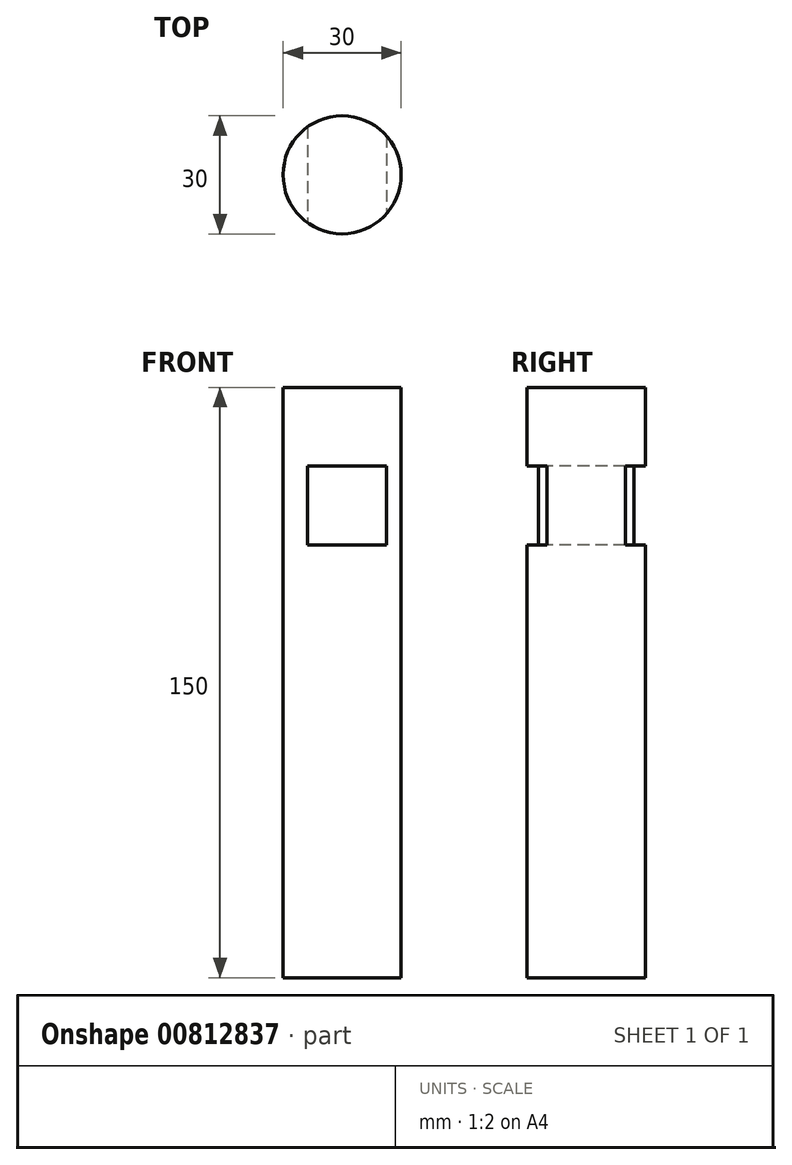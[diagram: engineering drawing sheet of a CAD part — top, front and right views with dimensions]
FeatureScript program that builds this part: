
annotation { "Feature Type Name" : "Feature", "Feature Type Description" : "" }
export const myFeature = defineFeature(function(context is Context, id is Id, definition is map)
    precondition{}
    {
        {
            var Q0;
            Q0=qCreatedBy(makeId("Top.planeOp"),FACE);
            var sketch = newSketch(context, id + "F0", { "sketchPlane" : qUnion([Q0])});
            skCircle(sketch, "E0", {"center": v(0, 0) * mm, "radius": 15 * mm});
            skSolve(sketch);
        }
        {
            var Q0;
            Q0=makeQuery(id+"F0.imprint","IMPRINT",FACE,{"disambiguationData":[TD([[makeQuery(id+"F0.imprint","IMPRINT",EDGE,{"derivedFrom":sQuery(id+"F0.wireOp",EDGE,"E0")}),1.0]])]});
            extrude(context, id + "F1", {"entities" : qUnion([Q0]), "depth" : 150 * mm, "offsetDistance" : 25 * mm});
        }
        {
            var Q0;
            Q0=qCreatedBy(makeId("Front.planeOp"),FACE);
            var sketch = newSketch(context, id + "F2", { "sketchPlane" : qUnion([Q0])});
            skLineSegment(sketch, "E1.bottom", {"start": v(-8.79, 130) * mm, "end": v(11.21, 130) * mm});
            skLineSegment(sketch, "E1.top", {"start": v(-8.79, 110) * mm, "end": v(11.21, 110) * mm});
            skLineSegment(sketch, "E1.left", {"start": v(-8.79, 130) * mm, "end": v(-8.79, 110) * mm});
            skLineSegment(sketch, "E1.right", {"start": v(11.21, 130) * mm, "end": v(11.21, 110) * mm});
            skSolve(sketch);
        }
        {
            var Q0;
            Q0 = qSketchRegion(id + "F2", true);
            extrude(context, id + "F3", {"entities" : qUnion([Q0]), "operationType" : NewBodyOperationType.REMOVE, "endBound" : BoundingType.UP_TO_NEXT, "oppositeDirection" : true, "depth" : 25 * mm, "offsetDistance" : 25 * mm});
        }
        {
            var Q0;
            Q0 = qSketchRegion(id + "F2", true);
            extrude(context, id + "F4", {"entities" : qUnion([Q0]), "operationType" : NewBodyOperationType.REMOVE, "endBound" : BoundingType.UP_TO_NEXT, "depth" : 25 * mm, "offsetDistance" : 25 * mm});
        }
    });
